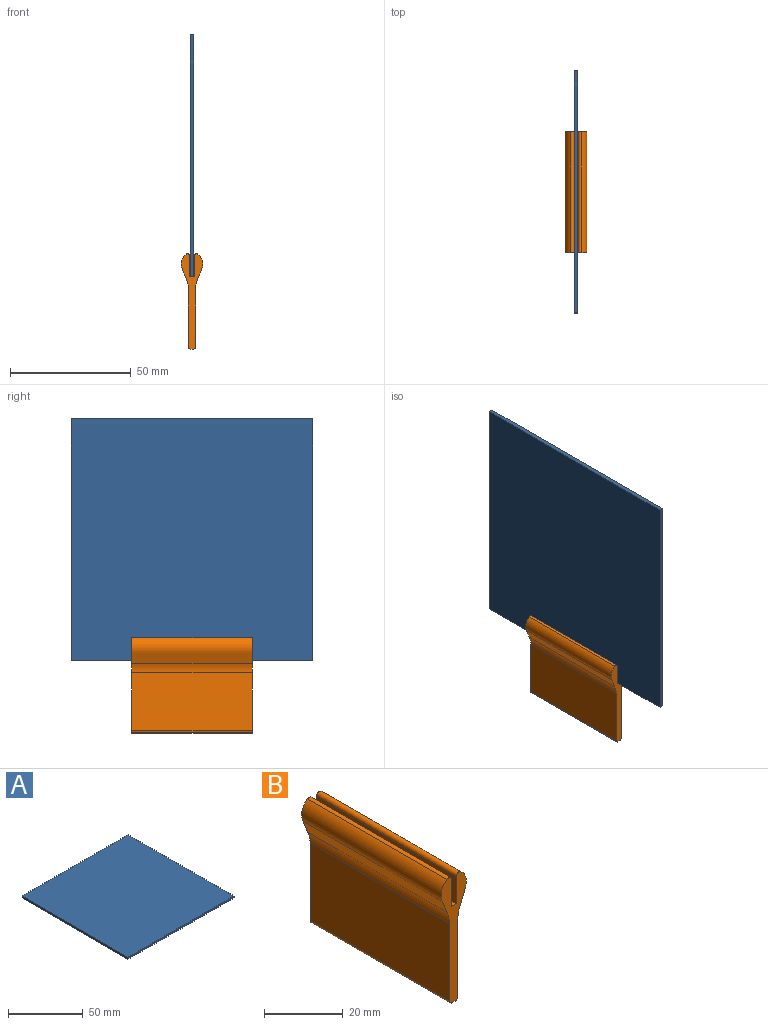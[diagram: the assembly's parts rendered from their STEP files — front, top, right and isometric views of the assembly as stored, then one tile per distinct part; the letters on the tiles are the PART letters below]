
ASSEMBLY  parts=2 mates=1
PART A: 6 faces, bbox 100x100x1.6 mm
  f0: plane 100x1.6mm, normal (0,-1,0), area 160mm2, adj f1,f3,f4,f5
  f1: plane 100x1.6mm, normal (1,0,0), area 160mm2, adj f0,f2,f4,f5
  f2: plane 100x1.6mm, normal (0,1,0), area 160mm2, adj f1,f3,f4,f5
  f3: plane 100x1.6mm, normal (-1,0,0), area 160mm2, adj f0,f2,f4,f5
  f4: plane 100x100mm, normal (0,0,1), area 10000mm2, adj f0,f1,f2,f3
  f5: plane 100x100mm, normal (0,0,-1), area 10000mm2, adj f0,f1,f2,f3
PART B: 18 faces, bbox 9.1x50x39.4 mm
  f0: plane 39.44x9.06mm, normal (0,-1,0), area 149.5mm2, adj f1,f2,f4,f5,f6,f7,f8,f9
  f1: plane 50x23.97mm, normal (1,0,0), area 1198.6mm2, adj f0,f3,f11,f16
  f2: plane 50x23.97mm, normal (-1,0,0), area 1198.6mm2, adj f0,f3,f10,f17
  f3: plane 39.44x9.06mm, normal (0,1,0), area 149.5mm2, adj f1,f2,f4,f5,f6,f7,f8,f9
  f4: plane 50x4.36mm, normal (-0.92,0,-0.39), area 236.8mm2, adj f0,f3,f10,f12
  f5: plane 50x4.36mm, normal (0.92,0,-0.39), area 236.8mm2, adj f0,f3,f11,f13
  f6: plane 50x8.44mm, normal (1,0,0), area 421.8mm2, adj f0,f3,f8,f15
  f7: plane 50x8.44mm, normal (-1,0,0), area 421.8mm2, adj f0,f3,f8,f14
  f8: plane 50x1.7mm, normal (0,0,1), area 85mm2, adj f0,f3,f6,f7
  f9: plane 50x1mm, normal (0,0,-1), area 50mm2, adj f0,f3,f16,f17
  f10: cylinder r=10mm len=50mm, axis (0,1,0), area 200.1mm2, adj f0,f2,f3,f4
  f11: cylinder r=10mm len=50mm, axis (0,1,0), area 200.1mm2, adj f0,f1,f3,f5
  f12: cylinder r=5mm len=50mm, axis (0,1,0), area 338.1mm2, adj f0,f3,f4,f15
  f13: cylinder r=5mm len=50mm, axis (0,1,0), area 338.1mm2, adj f0,f3,f5,f14
  f14: cylinder r=1mm len=50mm, axis (0,1,0), area 109.5mm2, adj f0,f3,f7,f13
  f15: cylinder r=1mm len=50mm, axis (0,1,0), area 109.5mm2, adj f0,f3,f6,f12
  f16: cylinder r=1mm len=50mm, axis (0,-1,0), area 78.5mm2, adj f0,f1,f3,f9
  f17: cylinder r=1mm len=50mm, axis (0,1,0), area 78.5mm2, adj f0,f2,f3,f9
PLACE A rot(axis=(0.71,0,0.71),180deg) t=(-0.8,25,57.22)mm
PLACE B t=(0,25,4.72)mm
MATE fastened A.f3 <-> B.f8  axis (0,0,-1) through (0,25,7.22)mm
